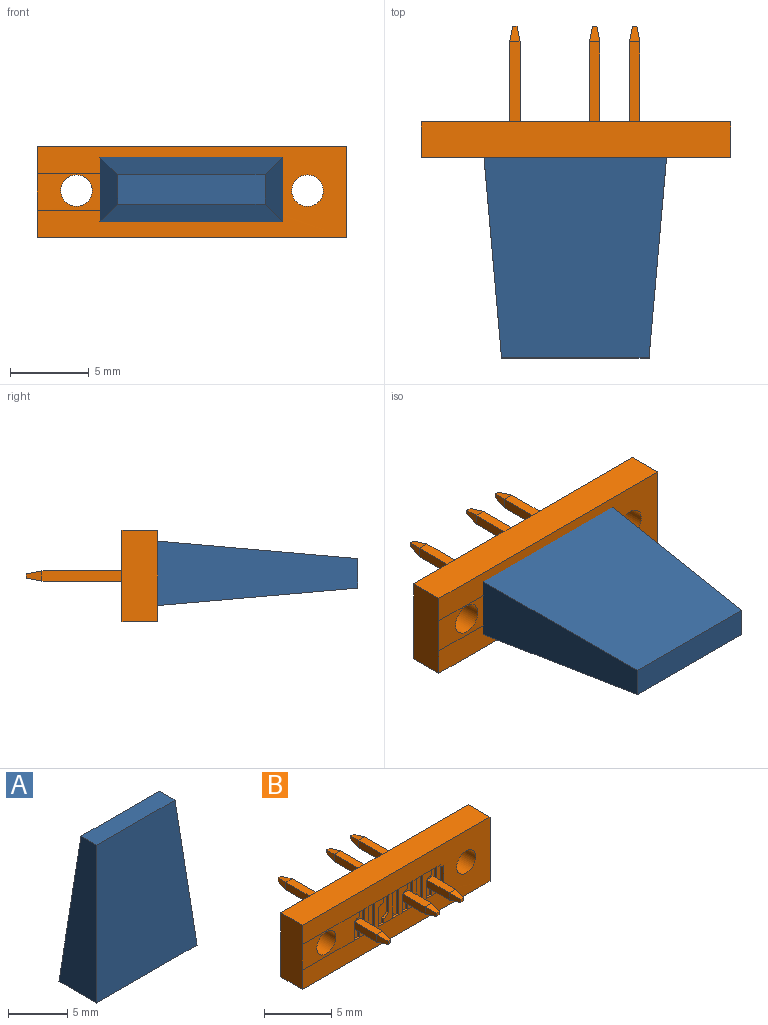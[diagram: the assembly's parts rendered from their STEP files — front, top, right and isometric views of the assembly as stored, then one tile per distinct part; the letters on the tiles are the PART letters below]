
ASSEMBLY  parts=2 mates=1
PART A: 11 faces, bbox 12x4.5x15 mm
  f0: plane 12x4.5mm, normal (0,0,-1), area 26.5mm2, adj f1,f2,f3,f4,f6,f7,f8,f9
  f1: plane 15x12mm, normal (0,-1,0.09), area 160.9mm2, adj f0,f2,f4,f5
  f2: plane 15x4.5mm, normal (1,0,0.09), area 48mm2, adj f0,f1,f3,f5
  f3: plane 15x12mm, normal (0,1,0.09), area 160.9mm2, adj f0,f2,f4,f5
  f4: plane 15x4.5mm, normal (-1,0,0.09), area 48mm2, adj f0,f1,f3,f5
  f5: plane 9.38x1.88mm, normal (0,0,1), area 17.6mm2, adj f1,f2,f3,f4
  f6: plane 14.1x10.19mm, normal (0,1,-0.09), area 126.8mm2, adj f0,f7,f9,f10
  f7: plane 14.1x2.69mm, normal (-1,0,-0.09), area 20.7mm2, adj f0,f6,f8,f10
  f8: plane 14.1x10.19mm, normal (0,-1,-0.09), area 126.8mm2, adj f0,f7,f9,f10
  f9: plane 14.1x2.69mm, normal (1,0,-0.09), area 20.7mm2, adj f0,f6,f8,f10
  f10: plane 7.73x0.23mm, normal (0,0,-1), area 1.7mm2, adj f6,f7,f8,f9
PART B: 212 faces, bbox 19.7x11.6x5.8 mm
  f0: plane 2.08x0.2mm, normal (1,0,0), area 0.4mm2, adj f1,f62,f106,f111,f206
  f1: plane 0.32x0.25mm, normal (0,-1,0), area 0.1mm2, adj f0,f108,f206,f208
  f2: plane 2.34x1.07mm, normal (0,-1,0), area 1.5mm2, adj f70,f71,f72,f74,f75,f76,f113,f118
  f3: plane 2.34x0.64mm, normal (0,-1,0), area 1.5mm2, adj f16,f17,f73,f84,f104,f105,f173,f183
  f4: plane 2.34x1.07mm, normal (0,-1,0), area 1.5mm2, adj f77,f78,f79,f81,f82,f83,f131,f136
  f5: plane 2.34x0.64mm, normal (0,-1,0), area 1.5mm2, adj f18,f19,f80,f92,f102,f103,f172,f185
  f6: plane 2.34x1.07mm, normal (0,-1,0), area 1.9mm2, adj f85,f86,f87,f89,f90,f91,f184,f204
  f7: plane 2.34x0.64mm, normal (0,-1,0), area 1.5mm2, adj f20,f21,f88,f99,f100,f101,f171,f187
  f8: plane 0.32x0.25mm, normal (0,1,0), area 0.1mm2, adj f23,f107,f191,f209
  f9: plane 2.34x1.42mm, normal (0,1,0), area 1.7mm2, adj f24,f33,f34,f35,f36,f37,f112,f117
  f10: plane 2.34x0.64mm, normal (0,1,0), area 1.5mm2, adj f16,f17,f38,f42,f104,f105,f173,f174
  f11: plane 2.34x1.42mm, normal (0,1,0), area 1.7mm2, adj f39,f40,f41,f43,f44,f45,f130,f135
  f12: plane 2.34x0.64mm, normal (0,1,0), area 1.5mm2, adj f18,f19,f46,f50,f102,f103,f172,f176
  f13: plane 2.34x1.42mm, normal (0,1,0), area 2.1mm2, adj f47,f48,f49,f51,f52,f53,f179,f196
  f14: plane 2.34x0.64mm, normal (0,1,0), area 1.5mm2, adj f20,f21,f54,f58,f100,f101,f171,f178
  f15: plane 2.34x1.42mm, normal (0,1,0), area 1.7mm2, adj f55,f56,f57,f59,f60,f61,f148,f153
  f16: plane 1.88x0.01mm, normal (-0.71,0,-0.71), area 0mm2, adj f3,f10,f17,f188
  f17: plane 1.88x0.01mm, normal (0.71,0,-0.71), area 0mm2, adj f3,f10,f16,f188
  f18: plane 1.88x0.01mm, normal (-0.71,0,-0.71), area 0mm2, adj f5,f12,f19,f189
  f19: plane 1.88x0.01mm, normal (0.71,0,-0.71), area 0mm2, adj f5,f12,f18,f189
  f20: plane 1.88x0.01mm, normal (0.71,0,-0.71), area 0mm2, adj f7,f14,f21,f190
  f21: plane 1.88x0.01mm, normal (-0.71,0,-0.71), area 0mm2, adj f7,f14,f20,f190
  f22: plane 2.34x1.07mm, normal (0,-1,0), area 1.5mm2, adj f93,f94,f95,f96,f97,f98,f149,f154
  f23: plane 2.08x0.2mm, normal (1,0,0), area 0.4mm2, adj f8,f25,f109,f110,f191
  f24: plane 0.68x0.2mm, normal (1,0,0), area 0.1mm2, adj f9,f26,f37,f175
  f25: plane 2.34x0.96mm, normal (0,1,0), area 1.2mm2, adj f23,f33,f34,f35,f168
  f26: plane 2.34x0.96mm, normal (0,1,0), area 1.2mm2, adj f24,f36,f37,f38,f168
  f27: plane 2.34x0.96mm, normal (0,1,0), area 1.2mm2, adj f39,f40,f41,f42,f168
  f28: plane 2.34x0.96mm, normal (0,1,0), area 1.2mm2, adj f43,f44,f45,f46,f168
  f29: plane 2.34x0.96mm, normal (0,1,0), area 1.2mm2, adj f47,f48,f49,f50,f168
  f30: plane 2.34x0.96mm, normal (0,1,0), area 1.2mm2, adj f51,f52,f53,f54,f168
  f31: plane 2.34x0.96mm, normal (0,1,0), area 1.2mm2, adj f55,f56,f57,f58,f168
  f32: plane 5.96x2.35mm, normal (0,1,0), area 9.7mm2, adj f59,f60,f61,f166,f168,f211
  f33: cylinder r=0.71mm len=1.2mm, axis (0,1,0), area 0.3mm2, adj f9,f25,f34,f35
  f34: plane 0.46x0.2mm, normal (-1,0,0), area 0.1mm2, adj f9,f25,f33,f175
  f35: plane 0.68x0.2mm, normal (-1,0,0), area 0.1mm2, adj f9,f25,f33,f192
  f36: plane 0.46x0.2mm, normal (1,0,0), area 0.1mm2, adj f9,f26,f37,f192
  f37: cylinder r=0.71mm len=1.2mm, axis (0,1,0), area 0.3mm2, adj f9,f24,f26,f36
  f38: plane 2.34x0.2mm, normal (-1,0,0), area 0.5mm2, adj f10,f26,f174,f193
  f39: plane 0.68x0.2mm, normal (-1,0,0), area 0.1mm2, adj f11,f27,f40,f194
  f40: cylinder r=0.71mm len=1.2mm, axis (0,1,0), area 0.3mm2, adj f11,f27,f39,f41
  f41: plane 0.46x0.2mm, normal (-1,0,0), area 0.1mm2, adj f11,f27,f40,f177
  f42: plane 2.34x0.2mm, normal (1,0,0), area 0.5mm2, adj f10,f27,f174,f193
  f43: plane 0.46x0.2mm, normal (1,0,0), area 0.1mm2, adj f11,f28,f44,f194
  f44: cylinder r=0.71mm len=1.2mm, axis (0,1,0), area 0.3mm2, adj f11,f28,f43,f45
  f45: plane 0.68x0.2mm, normal (1,0,0), area 0.1mm2, adj f11,f28,f44,f177
  f46: plane 2.34x0.2mm, normal (-1,0,0), area 0.5mm2, adj f12,f28,f176,f195
  f47: plane 0.68x0.2mm, normal (-1,0,0), area 0.1mm2, adj f13,f29,f48,f196
  f48: cylinder r=0.71mm len=1.2mm, axis (0,1,0), area 0.3mm2, adj f13,f29,f47,f49
  f49: plane 0.46x0.2mm, normal (-1,0,0), area 0.1mm2, adj f13,f29,f48,f179
  f50: plane 2.34x0.2mm, normal (1,0,0), area 0.5mm2, adj f12,f29,f176,f195
  f51: plane 0.46x0.2mm, normal (1,0,0), area 0.1mm2, adj f13,f30,f52,f196
  f52: cylinder r=0.71mm len=1.2mm, axis (0,1,0), area 0.3mm2, adj f13,f30,f51,f53
  f53: plane 0.68x0.2mm, normal (1,0,0), area 0.1mm2, adj f13,f30,f52,f179
  f54: plane 2.34x0.2mm, normal (-1,0,0), area 0.5mm2, adj f14,f30,f178,f197
  f55: plane 0.68x0.2mm, normal (-1,0,0), area 0.1mm2, adj f15,f31,f56,f198
  f56: cylinder r=0.71mm len=1.2mm, axis (0,1,0), area 0.3mm2, adj f15,f31,f55,f57
  f57: plane 0.46x0.2mm, normal (-1,0,0), area 0.1mm2, adj f15,f31,f56,f180
  f58: plane 2.34x0.2mm, normal (1,0,0), area 0.5mm2, adj f14,f31,f178,f197
  f59: plane 0.46x0.2mm, normal (1,0,0), area 0.1mm2, adj f15,f32,f60,f198
  f60: cylinder r=0.71mm len=1.2mm, axis (0,1,0), area 0.3mm2, adj f15,f32,f59,f61
  f61: plane 0.68x0.2mm, normal (1,0,0), area 0.1mm2, adj f15,f32,f60,f180
  f62: plane 2.34x0.96mm, normal (0,-1,0), area 1.3mm2, adj f0,f70,f71,f72,f169
  f63: plane 2.34x0.96mm, normal (0,-1,0), area 1.3mm2, adj f73,f74,f75,f76,f169
  f64: plane 2.34x0.96mm, normal (0,-1,0), area 1.3mm2, adj f77,f78,f79,f80,f169
  f65: plane 2.34x0.96mm, normal (0,-1,0), area 1.3mm2, adj f81,f82,f83,f84,f169
  f66: plane 2.34x0.96mm, normal (0,-1,0), area 1.3mm2, adj f85,f86,f87,f88,f169
  f67: plane 2.34x0.96mm, normal (0,-1,0), area 1.3mm2, adj f89,f90,f91,f92,f169
  f68: plane 5.96x2.34mm, normal (0,-1,0), area 9.8mm2, adj f93,f94,f95,f166,f169,f211
  f69: plane 2.34x0.96mm, normal (0,-1,0), area 1.3mm2, adj f96,f97,f98,f99,f169
  f70: plane 0.46x0.2mm, normal (-1,0,0), area 0.1mm2, adj f2,f62,f71,f199
  f71: cylinder r=0.71mm len=0.53mm, axis (0,-1,0), area 0.1mm2, adj f2,f62,f70,f72
  f72: plane 1.64x0.2mm, normal (-1,0,0), area 0.3mm2, adj f2,f62,f71,f181
  f73: plane 2.34x0.2mm, normal (-1,0,0), area 0.5mm2, adj f3,f63,f183,f200
  f74: plane 1.64x0.2mm, normal (1,0,0), area 0.3mm2, adj f2,f63,f75,f199
  f75: cylinder r=0.71mm len=0.53mm, axis (0,-1,0), area 0.1mm2, adj f2,f63,f74,f76
  f76: plane 0.46x0.2mm, normal (1,0,0), area 0.1mm2, adj f2,f63,f75,f181
  f77: plane 1.64x0.2mm, normal (1,0,0), area 0.3mm2, adj f4,f64,f78,f202
  f78: cylinder r=0.71mm len=0.53mm, axis (0,-1,0), area 0.1mm2, adj f4,f64,f77,f79
  f79: plane 0.46x0.2mm, normal (1,0,0), area 0.1mm2, adj f4,f64,f78,f182
  f80: plane 2.34x0.2mm, normal (-1,0,0), area 0.5mm2, adj f5,f64,f185,f201
  f81: plane 0.46x0.2mm, normal (-1,0,0), area 0.1mm2, adj f4,f65,f82,f202
  f82: cylinder r=0.71mm len=0.53mm, axis (0,-1,0), area 0.1mm2, adj f4,f65,f81,f83
  f83: plane 1.64x0.2mm, normal (-1,0,0), area 0.3mm2, adj f4,f65,f82,f182
  f84: plane 2.34x0.2mm, normal (1,0,0), area 0.5mm2, adj f3,f65,f183,f200
  f85: plane 1.64x0.2mm, normal (1,0,0), area 0.3mm2, adj f6,f66,f86,f204
  f86: cylinder r=0.71mm len=0.53mm, axis (0,-1,0), area 0.1mm2, adj f6,f66,f85,f87
  f87: plane 0.46x0.2mm, normal (1,0,0), area 0.1mm2, adj f6,f66,f86,f184
  f88: plane 2.34x0.2mm, normal (-1,0,0), area 0.5mm2, adj f7,f66,f187,f203
  f89: plane 0.46x0.2mm, normal (-1,0,0), area 0.1mm2, adj f6,f67,f90,f204
  f90: cylinder r=0.71mm len=0.53mm, axis (0,-1,0), area 0.1mm2, adj f6,f67,f89,f91
  f91: plane 1.64x0.2mm, normal (-1,0,0), area 0.3mm2, adj f6,f67,f90,f184
  f92: plane 2.34x0.2mm, normal (1,0,0), area 0.5mm2, adj f5,f67,f185,f201
  f93: plane 1.64x0.2mm, normal (1,0,0), area 0.3mm2, adj f22,f68,f94,f205
  f94: cylinder r=0.71mm len=0.53mm, axis (0,-1,0), area 0.1mm2, adj f22,f68,f93,f95
  f95: plane 0.46x0.2mm, normal (1,0,0), area 0.1mm2, adj f22,f68,f94,f186
  f96: plane 0.46x0.2mm, normal (-1,0,0), area 0.1mm2, adj f22,f69,f97,f205
  f97: cylinder r=0.71mm len=0.53mm, axis (0,-1,0), area 0.1mm2, adj f22,f69,f96,f98
  f98: plane 1.64x0.2mm, normal (-1,0,0), area 0.3mm2, adj f22,f69,f97,f186
  f99: plane 2.34x0.2mm, normal (1,0,0), area 0.5mm2, adj f7,f69,f187,f203
  f100: plane 1.88x0.01mm, normal (0.71,0,0.71), area 0mm2, adj f7,f14,f101,f171
  f101: plane 1.88x0.01mm, normal (-0.71,0,0.71), area 0mm2, adj f7,f14,f100,f171
  f102: plane 1.88x0.01mm, normal (0.71,0,0.71), area 0mm2, adj f5,f12,f103,f172
  f103: plane 1.88x0.01mm, normal (-0.71,0,0.71), area 0mm2, adj f5,f12,f102,f172
  f104: plane 1.88x0.01mm, normal (0.71,0,0.71), area 0mm2, adj f3,f10,f105,f173
  f105: plane 1.88x0.01mm, normal (-0.71,0,0.71), area 0mm2, adj f3,f10,f104,f173
  f106: plane 1.83x0.38mm, normal (0.77,-0.64,0), area 0.9mm2, adj f0,f108,f111,f208
  f107: plane 0.38x0.32mm, normal (0,0,1), area 0.1mm2, adj f8,f109,f209
  f108: plane 0.38x0.32mm, normal (0,0,1), area 0.1mm2, adj f1,f106,f208
  f109: plane 1.83x0.38mm, normal (0.77,0.64,0), area 0.9mm2, adj f23,f107,f110,f209
  f110: plane 0.58x0.32mm, normal (0,0,-1), area 0.1mm2, adj f23,f109,f168,f209
  f111: plane 0.58x0.32mm, normal (0,0,-1), area 0.1mm2, adj f0,f106,f169,f208
  f112: plane 5.28x0.66mm, normal (-1,0,0), area 3.5mm2, adj f9,f114,f117,f123
  f113: plane 2.36x0.66mm, normal (-1,0,0), area 1.6mm2, adj f2,f118,f124,f129
  f114: plane 1.02x0.66mm, normal (-0.98,0.18,0), area 0.5mm2, adj f112,f115,f116,f122
  f115: plane 0.28x0.28mm, normal (0,1,0), area 0.1mm2, adj f114,f116,f121,f122
  f116: plane 1.02x0.66mm, normal (0,0.18,-0.98), area 0.5mm2, adj f114,f115,f117,f121
  f117: plane 5.28x0.66mm, normal (0,0,-1), area 3.5mm2, adj f9,f112,f116,f119
  f118: plane 2.36x0.66mm, normal (0,0,-1), area 1.6mm2, adj f2,f113,f120,f128
  f119: plane 5.28x0.66mm, normal (1,0,0), area 3.5mm2, adj f9,f117,f121,f123
  f120: plane 2.36x0.66mm, normal (1,0,0), area 1.6mm2, adj f2,f118,f124,f126
  f121: plane 1.02x0.66mm, normal (0.98,0.18,0), area 0.5mm2, adj f115,f116,f119,f122
  f122: plane 1.02x0.66mm, normal (0,0.18,0.98), area 0.5mm2, adj f114,f115,f121,f123
  f123: plane 5.28x0.66mm, normal (0,0,1), area 3.5mm2, adj f9,f112,f119,f122
  f124: plane 2.36x0.66mm, normal (0,0,1), area 1.6mm2, adj f2,f113,f120,f125
  f125: plane 1.02x0.66mm, normal (0,-0.18,0.98), area 0.5mm2, adj f124,f126,f127,f129
  f126: plane 1.02x0.66mm, normal (0.98,-0.18,0), area 0.5mm2, adj f120,f125,f127,f128
  f127: plane 0.28x0.28mm, normal (0,-1,0), area 0.1mm2, adj f125,f126,f128,f129
  f128: plane 1.02x0.66mm, normal (0,-0.18,-0.98), area 0.5mm2, adj f118,f126,f127,f129
  f129: plane 1.02x0.66mm, normal (-0.98,-0.18,0), area 0.5mm2, adj f113,f125,f127,f128
  f130: plane 5.28x0.66mm, normal (-1,0,0), area 3.5mm2, adj f11,f132,f135,f141
  f131: plane 2.36x0.66mm, normal (-1,0,0), area 1.6mm2, adj f4,f136,f142,f147
  f132: plane 1.02x0.66mm, normal (-0.98,0.18,0), area 0.5mm2, adj f130,f133,f134,f140
  f133: plane 0.28x0.28mm, normal (0,1,0), area 0.1mm2, adj f132,f134,f139,f140
  f134: plane 1.02x0.66mm, normal (0,0.18,-0.98), area 0.5mm2, adj f132,f133,f135,f139
  f135: plane 5.28x0.66mm, normal (0,0,-1), area 3.5mm2, adj f11,f130,f134,f137
  f136: plane 2.36x0.66mm, normal (0,0,-1), area 1.6mm2, adj f4,f131,f138,f146
  f137: plane 5.28x0.66mm, normal (1,0,0), area 3.5mm2, adj f11,f135,f139,f141
  f138: plane 2.36x0.66mm, normal (1,0,0), area 1.6mm2, adj f4,f136,f142,f144
  f139: plane 1.02x0.66mm, normal (0.98,0.18,0), area 0.5mm2, adj f133,f134,f137,f140
  f140: plane 1.02x0.66mm, normal (0,0.18,0.98), area 0.5mm2, adj f132,f133,f139,f141
  f141: plane 5.28x0.66mm, normal (0,0,1), area 3.5mm2, adj f11,f130,f137,f140
  f142: plane 2.36x0.66mm, normal (0,0,1), area 1.6mm2, adj f4,f131,f138,f143
  f143: plane 1.02x0.66mm, normal (0,-0.18,0.98), area 0.5mm2, adj f142,f144,f145,f147
  f144: plane 1.02x0.66mm, normal (0.98,-0.18,0), area 0.5mm2, adj f138,f143,f145,f146
  f145: plane 0.28x0.28mm, normal (0,-1,0), area 0.1mm2, adj f143,f144,f146,f147
  f146: plane 1.02x0.66mm, normal (0,-0.18,-0.98), area 0.5mm2, adj f136,f144,f145,f147
  f147: plane 1.02x0.66mm, normal (-0.98,-0.18,0), area 0.5mm2, adj f131,f143,f145,f146
  f148: plane 5.28x0.66mm, normal (-1,0,0), area 3.5mm2, adj f15,f150,f153,f159
  f149: plane 2.36x0.66mm, normal (-1,0,0), area 1.6mm2, adj f22,f154,f160,f165
  f150: plane 1.02x0.66mm, normal (-0.98,0.18,0), area 0.5mm2, adj f148,f151,f152,f158
  f151: plane 0.28x0.28mm, normal (0,1,0), area 0.1mm2, adj f150,f152,f157,f158
  f152: plane 1.02x0.66mm, normal (0,0.18,-0.98), area 0.5mm2, adj f150,f151,f153,f157
  f153: plane 5.28x0.66mm, normal (0,0,-1), area 3.5mm2, adj f15,f148,f152,f155
  f154: plane 2.36x0.66mm, normal (0,0,-1), area 1.6mm2, adj f22,f149,f156,f164
  f155: plane 5.28x0.66mm, normal (1,0,0), area 3.5mm2, adj f15,f153,f157,f159
  f156: plane 2.36x0.66mm, normal (1,0,0), area 1.6mm2, adj f22,f154,f160,f162
  f157: plane 1.02x0.66mm, normal (0.98,0.18,0), area 0.5mm2, adj f151,f152,f155,f158
  f158: plane 1.02x0.66mm, normal (0,0.18,0.98), area 0.5mm2, adj f150,f151,f157,f159
  f159: plane 5.28x0.66mm, normal (0,0,1), area 3.5mm2, adj f15,f148,f155,f158
  f160: plane 2.36x0.66mm, normal (0,0,1), area 1.6mm2, adj f22,f149,f156,f161
  f161: plane 1.02x0.66mm, normal (0,-0.18,0.98), area 0.5mm2, adj f160,f162,f163,f165
  f162: plane 1.02x0.66mm, normal (0.98,-0.18,0), area 0.5mm2, adj f156,f161,f163,f164
  f163: plane 0.28x0.28mm, normal (0,-1,0), area 0.1mm2, adj f161,f162,f164,f165
  f164: plane 1.02x0.66mm, normal (0,-0.18,-0.98), area 0.5mm2, adj f154,f162,f163,f165
  f165: plane 1.02x0.66mm, normal (-0.98,-0.18,0), area 0.5mm2, adj f149,f161,f163,f164
  f166: plane 5.83x2.29mm, normal (-1,0,0), area 13.3mm2, adj f32,f68,f167,f168,f169,f170
  f167: plane 19.68x2.28mm, normal (0,0,1), area 44.9mm2, adj f166,f168,f169,f207
  f168: plane 19.69x5.84mm, normal (0,1,0), area 77mm2, adj f25,f26,f27,f28,f29,f30,f31,f32
  f169: plane 19.69x5.84mm, normal (0,-1,0), area 77mm2, adj f62,f63,f64,f65,f66,f67,f68,f69
  f170: plane 19.68x2.28mm, normal (0,0,-1), area 44.9mm2, adj f166,f168,f169,f207
  f171: plane 1.88x0.03mm, normal (0,0,-1), area 0mm2, adj f7,f14,f100,f101
  f172: plane 1.88x0.03mm, normal (0,0,-1), area 0mm2, adj f5,f12,f102,f103
  f173: plane 1.88x0.03mm, normal (0,0,-1), area 0mm2, adj f3,f10,f104,f105
  f174: plane 0.64x0.2mm, normal (0,0,-1), area 0.1mm2, adj f10,f38,f42,f168
  f175: plane 0.52x0.2mm, normal (0,0,-1), area 0.1mm2, adj f9,f24,f34,f168
  f176: plane 0.64x0.2mm, normal (0,0,-1), area 0.1mm2, adj f12,f46,f50,f168
  f177: plane 0.52x0.2mm, normal (0,0,-1), area 0.1mm2, adj f11,f41,f45,f168
  f178: plane 0.64x0.2mm, normal (0,0,-1), area 0.1mm2, adj f14,f54,f58,f168
  f179: plane 0.52x0.2mm, normal (0,0,-1), area 0.1mm2, adj f13,f49,f53,f168
  f180: plane 0.52x0.2mm, normal (0,0,-1), area 0.1mm2, adj f15,f57,f61,f168
  f181: plane 0.53x0.2mm, normal (0,0,-1), area 0.1mm2, adj f2,f72,f76,f169
  f182: plane 0.53x0.2mm, normal (0,0,-1), area 0.1mm2, adj f4,f79,f83,f169
  f183: plane 0.64x0.2mm, normal (0,0,-1), area 0.1mm2, adj f3,f73,f84,f169
  f184: plane 0.53x0.2mm, normal (0,0,-1), area 0.1mm2, adj f6,f87,f91,f169
  f185: plane 0.64x0.2mm, normal (0,0,-1), area 0.1mm2, adj f5,f80,f92,f169
  f186: plane 0.53x0.2mm, normal (0,0,-1), area 0.1mm2, adj f22,f95,f98,f169
  f187: plane 0.64x0.2mm, normal (0,0,-1), area 0.1mm2, adj f7,f88,f99,f169
  f188: plane 1.88x0.03mm, normal (0,0,1), area 0mm2, adj f3,f10,f16,f17
  f189: plane 1.88x0.03mm, normal (0,0,1), area 0mm2, adj f5,f12,f18,f19
  f190: plane 1.88x0.03mm, normal (0,0,1), area 0mm2, adj f7,f14,f20,f21
  f191: plane 0.32x0.2mm, normal (0,0,1), area 0.1mm2, adj f8,f23,f168,f209
  f192: plane 0.52x0.2mm, normal (0,0,1), area 0.1mm2, adj f9,f35,f36,f168
  f193: plane 0.64x0.2mm, normal (0,0,1), area 0.1mm2, adj f10,f38,f42,f168
  f194: plane 0.52x0.2mm, normal (0,0,1), area 0.1mm2, adj f11,f39,f43,f168
  f195: plane 0.64x0.2mm, normal (0,0,1), area 0.1mm2, adj f12,f46,f50,f168
  f196: plane 0.52x0.2mm, normal (0,0,1), area 0.1mm2, adj f13,f47,f51,f168
  f197: plane 0.64x0.2mm, normal (0,0,1), area 0.1mm2, adj f14,f54,f58,f168
  f198: plane 0.52x0.2mm, normal (0,0,1), area 0.1mm2, adj f15,f55,f59,f168
  f199: plane 0.53x0.2mm, normal (0,0,1), area 0.1mm2, adj f2,f70,f74,f169
  f200: plane 0.64x0.2mm, normal (0,0,1), area 0.1mm2, adj f3,f73,f84,f169
  f201: plane 0.64x0.2mm, normal (0,0,1), area 0.1mm2, adj f5,f80,f92,f169
  f202: plane 0.53x0.2mm, normal (0,0,1), area 0.1mm2, adj f4,f77,f81,f169
  f203: plane 0.64x0.2mm, normal (0,0,1), area 0.1mm2, adj f7,f88,f99,f169
  f204: plane 0.53x0.2mm, normal (0,0,1), area 0.1mm2, adj f6,f85,f89,f169
  f205: plane 0.53x0.2mm, normal (0,0,1), area 0.1mm2, adj f22,f93,f96,f169
  f206: plane 0.32x0.2mm, normal (0,0,1), area 0.1mm2, adj f0,f1,f169,f208
  f207: plane 5.83x2.28mm, normal (1,0,0), area 13.3mm2, adj f167,f168,f169,f170
  f208: plane 2.08x0.58mm, normal (-1,0,0), area 1.1mm2, adj f1,f106,f108,f111,f169,f206
  f209: plane 2.08x0.58mm, normal (-1,0,0), area 1.1mm2, adj f8,f107,f109,f110,f168,f191
  f210: cylinder r=1mm len=2.28mm, axis (0,1,0), area 14.3mm2, adj f168,f169
  f211: cylinder r=1mm len=2.29mm, axis (0,1,0), area 14.3mm2, adj f32,f68
PLACE A rot(axis=(1,0,0),90deg) t=(0.03,1.14,0.17)mm
PLACE B at identity
MATE planar A.f0 <-> B.f27  axis (0,1,0) through (0.03,1.14,0.17)mm
